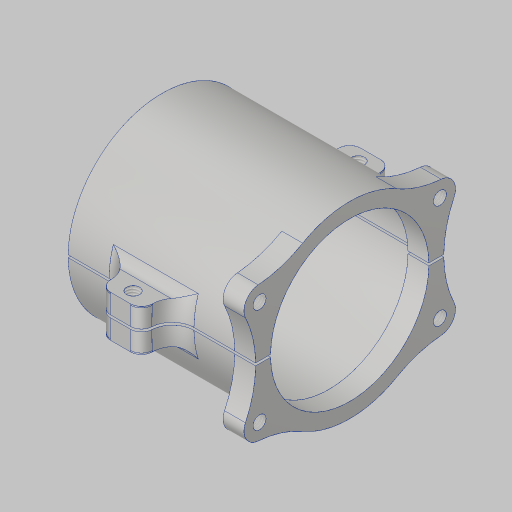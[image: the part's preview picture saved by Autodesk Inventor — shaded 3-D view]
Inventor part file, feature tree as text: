
AUTODESK INVENTOR PART (.ipt)
format: ipt  version: 2023.5 (Build 275446000, 446)  size: 449,536 bytes
history: native  units: in
note: dims shown in document units (in); Inventor stores cm internally (conversion verified against a paired STEP export)
features: sketch x9, extrude x7, projected_geometry x5, hole x2, fillet x2, plane x1, mirror x1, split x1
ambient origin geometry x8: Origin, YZ Plane, XZ Plane, XY Plane, X Axis, Y Axis, Z Axis, Center Point
bodies: Solid1 (feature_tree), Solid2 (feature_tree), Solid3 (feature_tree)
feature tree (28):
  extrude  "Extrusion1"  Depth=0.1in
  extrude  "Extrusion2"  Depth=3.0in
  hole  "Hole1"  [1 undecoded]
  plane  "Work Plane2"
  extrude  "Extrusion4"  Depth=3.0in
  mirror  "Mirror1"
  fillet  "Fillet1"  Radius=1.5in
  fillet  "Fillet2"  Radius=0.5in
  hole  "Hole2"  [1 undecoded]
  extrude  "Extrusion5"  Depth=0.26in
  extrude  "Extrusion6"  Depth=1.9in
  split  "Split1"
  extrude  "Extrusion7"  Depth=0.015in TaperAngle=0.0deg
  extrude  "Extrusion8"  Depth=0.015in
  sketch  "Sketch1"  dims[d0=2.06in d1=0.1in]
  sketch  "Sketch2"  dims[d2=2.0in d3=0.0in d4=3.0in]
  sketch  "Sketch3"  dims[d5=3.0in d6=0.25in d7=0.0in]
  sketch  "Sketch6"  dims[d9=2.3622in d11=360.0deg]
  sketch  "Sketch7"  dims[d13=0.156in d14=0.38in d15=0.375in d16=0.25in d17=0.5635in d18=1.0in d19=0.8108in d20=3.0in d22=1.5in d27=0.5in]
  sketch  "Sketch8"  dims[d28=0.5in d29=0.45in d30=0.0in]
  sketch  "Sketch9"  dims[d31=0.26in d32=0.13in]
  projected_geometry  "Projected Loop1"
  projected_geometry  "Projected Loop2"
  sketch  "Sketch10"  dims[d35=0.156in d36=0.38in d37=0.375in d38=0.25in d39=0.5635in d40=1.0in d41=0.8108in d42=1.9in]
  sketch  "Sketch11"  dims[d43=0.375in d44=0.25in d45=0.0in d46=2.5in d47=0.0in d48=0.0in d57=0.015in d58=0.0in d59=0.015in d60=0.0in d33=0.0in d34=0.0in]
  projected_geometry  "Project Cut Edges1"
  projected_geometry  "Project Cut Edges2"
  projected_geometry  "Project Cut Edges3"
note: 2 required parameter values undecoded (feature->parameter linkage not recoverable at this tier; creation-order binding heuristic only, values carry confidence <= 0.55)
